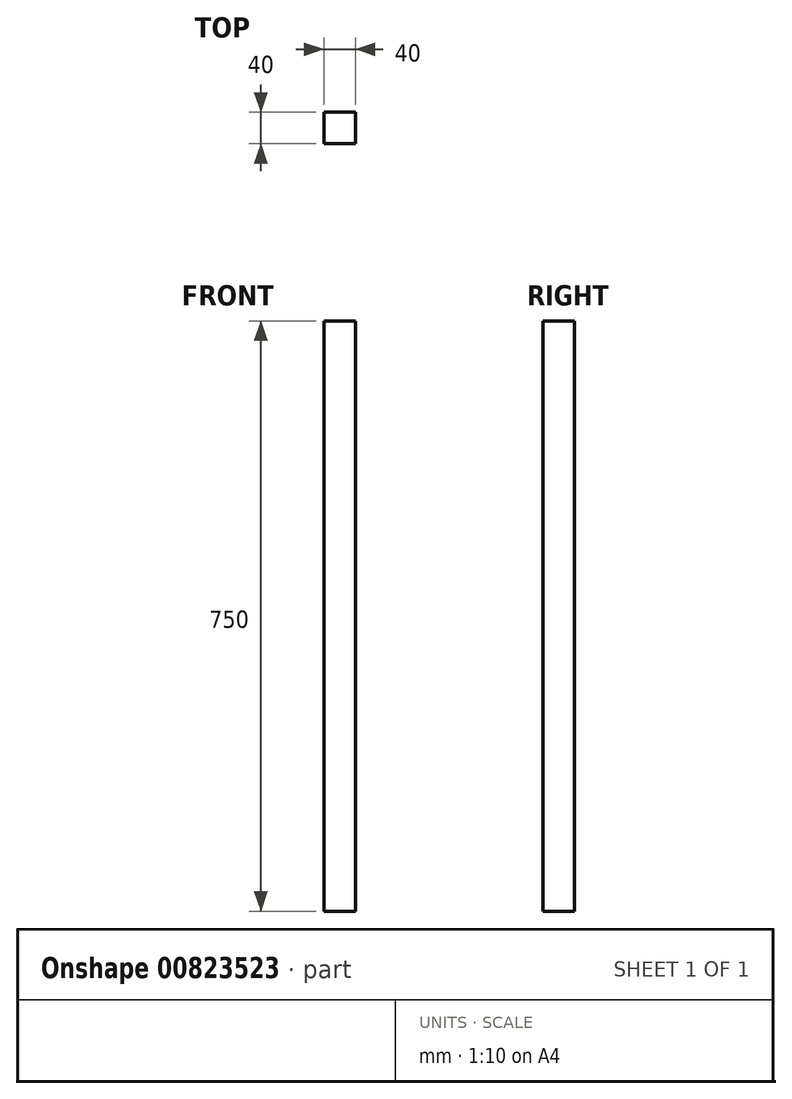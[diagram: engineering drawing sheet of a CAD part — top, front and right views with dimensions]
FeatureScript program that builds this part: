
annotation { "Feature Type Name" : "Feature", "Feature Type Description" : "" }
export const myFeature = defineFeature(function(context is Context, id is Id, definition is map)
    precondition{}
    {
        {
            var Q0;
            Q0=qCreatedBy(makeId("Top.planeOp"),FACE);
            var sketch = newSketch(context, id + "F0", { "sketchPlane" : qUnion([Q0])});
            skLineSegment(sketch, "E0.bottom", {"start": v(20, -20) * mm, "end": v(-20, -20) * mm});
            skLineSegment(sketch, "E0.top", {"start": v(20, 20) * mm, "end": v(-20, 20) * mm});
            skLineSegment(sketch, "E0.left", {"start": v(20, -20) * mm, "end": v(20, 20) * mm});
            skLineSegment(sketch, "E0.right", {"start": v(-20, -20) * mm, "end": v(-20, 20) * mm});
            skPoint(sketch, "E0.middle", {"position": v(0, 0) * mm});
            skSolve(sketch);
        }
        {
            var Q0;
            Q0=makeQuery(id+"F0.imprint","IMPRINT",FACE,{"disambiguationData":[TD([[makeQuery(id+"F0.imprint","IMPRINT",EDGE,{"derivedFrom":sQuery(id+"F0.wireOp",EDGE,"E0.bottom")}),-1.0]])]});
            extrude(context, id + "F1", {"entities" : qUnion([Q0]), "depth" : 750 * mm, "offsetDistance" : 25 * mm});
        }
    });
